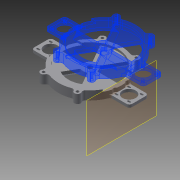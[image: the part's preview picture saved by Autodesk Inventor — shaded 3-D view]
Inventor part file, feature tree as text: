
AUTODESK INVENTOR PART (.ipt)
format: ipt  version: 2014 SP2 (Build 180246200, 246)  size: 536,576 bytes
history: native  units: mm
features: sketch x16, extrude x13, reference x9, fillet x4, mirror x3, projected_geometry x3, pattern_circular x2, hole x2, chamfer x2, plane x1
ambient origin geometry x8: Origin, YZ Plane, XZ Plane, XY Plane, X Axis, Y Axis, Z Axis, Center Point
bodies: Solid1 (feature_tree)
feature tree (55):
  extrude  "Extrusion1"  Depth=10.0mm TaperAngle=0.0deg
  extrude  "Extrusion3"  Depth=7.0mm
  pattern_circular  "Circular Pattern1"  Count=3 Angle=360.0deg
  extrude  "Extrusion4"  Depth=6.0mm TaperAngle=0.0deg
  extrude  "Extrusion5"  Depth=2.0mm
  hole  "Hole1"  [1 undecoded]
  sketch  "Sketch8"  dims[d15=4.0mm d16=0.0mm d23=6.0mm d24=0.0mm]
  plane  "Work Plane2"
  extrude  "Extrusion6"  TaperAngle=0.0deg  [1 undecoded]
  fillet  "Fillet2"  Radius=93.0mm
  extrude  "Extrusion7"  TaperAngle=0.0deg  [1 undecoded]
  extrude  "Extrusion8"  Depth=2.0mm
  extrude  "Extrusion10"  Depth=5.0mm
  extrude  "Extrusion11"  Depth=32.0mm TaperAngle=0.0deg
  extrude  "Extrusion12"  Depth=1.5mm
  fillet  "Fillet3"  Radius=3.0mm
  fillet  "Fillet4"  Radius=1.5mm
  extrude  "Extrusion13"  Depth=1.5mm
  mirror  "Mirror1"
  chamfer  "Chamfer3"  Distance=1.5mm
  extrude  "Extrusion14"  Depth=1.5mm
  hole  "Hole2"  [1 undecoded]
  fillet  "Fillet5"  [1 undecoded]
  mirror  "Mirror2"
  mirror  "Mirror3"
  extrude  "Extrusion15"  Depth=2.0mm TaperAngle=45.0deg
  chamfer  "Chamfer4"  Distance=8.0mm
  pattern_circular  "Circular Pattern2"  [2 undecoded]
  sketch  "Sketch1"  dims[d0=115.0mm d1=10.0mm d2=0.0mm]
  sketch  "Sketch3"  dims[d6=7.0mm d7=25.0mm]
  sketch  "Sketch4"  dims[d8=60.0deg]
  sketch  "Sketch6"  dims[d9=38.0mm]
  sketch  "Sketch7"  dims[d10=5.0mm d11=0.0mm d12=30.0mm d13=360.0deg]
  sketch  "Sketch10"  dims[d25=9.0mm d26=6.0mm d27=4.0mm d28=2.0mm d29=90.0deg d30=8.0mm d31=20.594885mm d32=2.0mm]
  reference  "Reference8"
  reference  "Reference9"
  projected_geometry  "Projected Loop3"
  projected_geometry  "Projected Loop4"
  sketch  "Sketch11"  dims[d33=2.0mm d34=28.2mm]
  reference  "Reference10"
  sketch  "Sketch12"  dims[d35=28.2mm d37=0.0mm d39=93.0mm]
  projected_geometry  "Projected Loop5"
  sketch  "Sketch14"  dims[d41=0.0mm d42=0.0mm]
  reference  "Reference11"
  reference  "Reference12"
  reference  "Reference13"
  reference  "Reference14"
  sketch  "Sketch15"  dims[d43=70.0mm d44=0.0mm d52=2.0mm]
  sketch  "Sketch16"  dims[d53=35.0mm d54=5.0mm]
  sketch  "Sketch17"  dims[d55=0.0mm d56=32.0mm d57=0.0mm]
  reference  "Reference15"
  sketch  "Sketch18"  dims[d58=32.0mm d59=0.0mm d63=1.5mm d64=3.0mm d65=1.5mm]
  sketch  "Sketch19"  dims[d66=3.0mm d67=1.5mm]
  sketch  "Sketch20"  dims[d68=3.0mm d69=1.5mm d70=1.5mm d71=2.0mm d72=0.0mm d73=0.0mm d74=0.0mm d75=6.5mm d76=2.0mm d77=45.0deg d78=8.0mm d79=8.0mm d80=2.0mm d81=0.0mm d82=5.0mm d83=3.0mm d84=1.0mm d85=2.0mm d86=0.0mm d88=0.872665mm d89=10.0mm d90=0.872665mm d91=2.0mm d92=0.0mm d93=5.0mm d94=6.0mm d95=4.0mm d96=2.0mm d97=90.0deg d98=8.0mm d99=20.594885mm d100=10.0mm d101=5.0mm d102=2.0mm d103=0.0mm d104=11.0mm d105=2.0mm d106=4.886922mm d107=30.0mm d108=360.0deg]
  reference  "Reference16"
note: 7 required parameter values undecoded (feature->parameter linkage not recoverable at this tier; creation-order binding heuristic only, values carry confidence <= 0.55)
